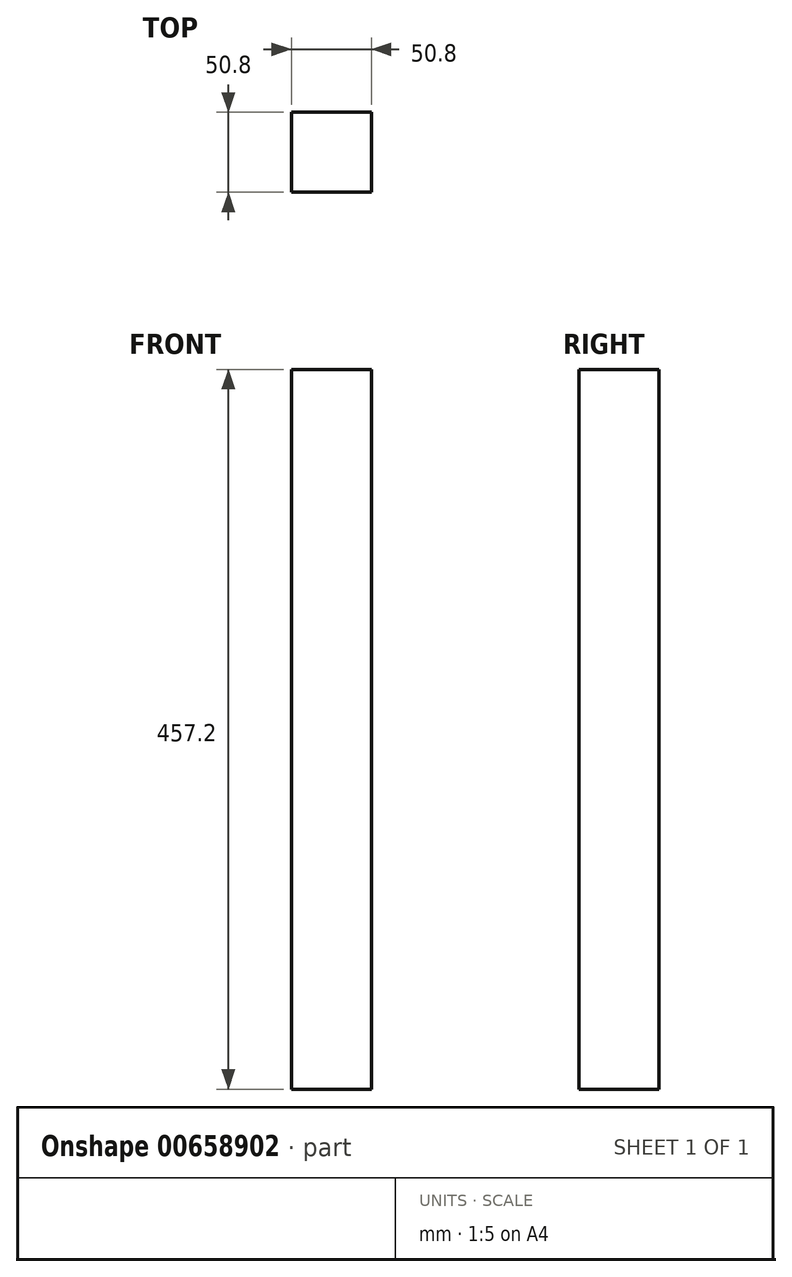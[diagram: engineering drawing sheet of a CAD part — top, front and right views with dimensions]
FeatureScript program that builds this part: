
annotation { "Feature Type Name" : "Feature", "Feature Type Description" : "" }
export const myFeature = defineFeature(function(context is Context, id is Id, definition is map)
    precondition{}
    {
        {
            var Q0;
            Q0=qCreatedBy(makeId("Top.planeOp"),FACE);
            var sketch = newSketch(context, id + "F0", { "sketchPlane" : qUnion([Q0])});
            skLineSegment(sketch, "E0.bottom", {"start": v(25.4, 25.4) * mm, "end": v(-25.4, 25.4) * mm});
            skLineSegment(sketch, "E0.top", {"start": v(25.4, -25.4) * mm, "end": v(-25.4, -25.4) * mm});
            skLineSegment(sketch, "E0.left", {"start": v(25.4, 25.4) * mm, "end": v(25.4, -25.4) * mm});
            skLineSegment(sketch, "E0.right", {"start": v(-25.4, 25.4) * mm, "end": v(-25.4, -25.4) * mm});
            skPoint(sketch, "E0.middle", {"position": v(0, 0) * mm});
            skSolve(sketch);
        }
        {
            var Q0;
            Q0=makeQuery(id+"F0.imprint","IMPRINT",FACE,{"disambiguationData":[TD([[makeQuery(id+"F0.imprint","IMPRINT",EDGE,{"derivedFrom":sQuery(id+"F0.wireOp",EDGE,"E0.bottom")}),1.0]])]});
            extrude(context, id + "F1", {"entities" : qUnion([Q0]), "oppositeDirection" : true, "depth" : 457.2 * mm, "offsetDistance" : 25.4 * mm});
        }
        {
            var Q0;
            Q0=qCreatedBy(makeId("Right.planeOp"),FACE);
            var sketch = newSketch(context, id + "F2", { "sketchPlane" : qUnion([Q0])});
            skLineSegment(sketch, "E1", {"start": v(0, -457.2) * mm, "end": v(25.4, -127) * mm});
            skLineSegment(sketch, "E2", {"start": v(25.4, -127) * mm, "end": v(25.4, -457.2) * mm});
            skLineSegment(sketch, "E3", {"start": v(25.4, -457.2) * mm, "end": v(0, -457.2) * mm});
            skLineSegment(sketch, "E4", {"start": v(0, -457.2) * mm, "end": v(0, 125.08) * mm, "construction": true});
            skSolve(sketch);
        }
    });
